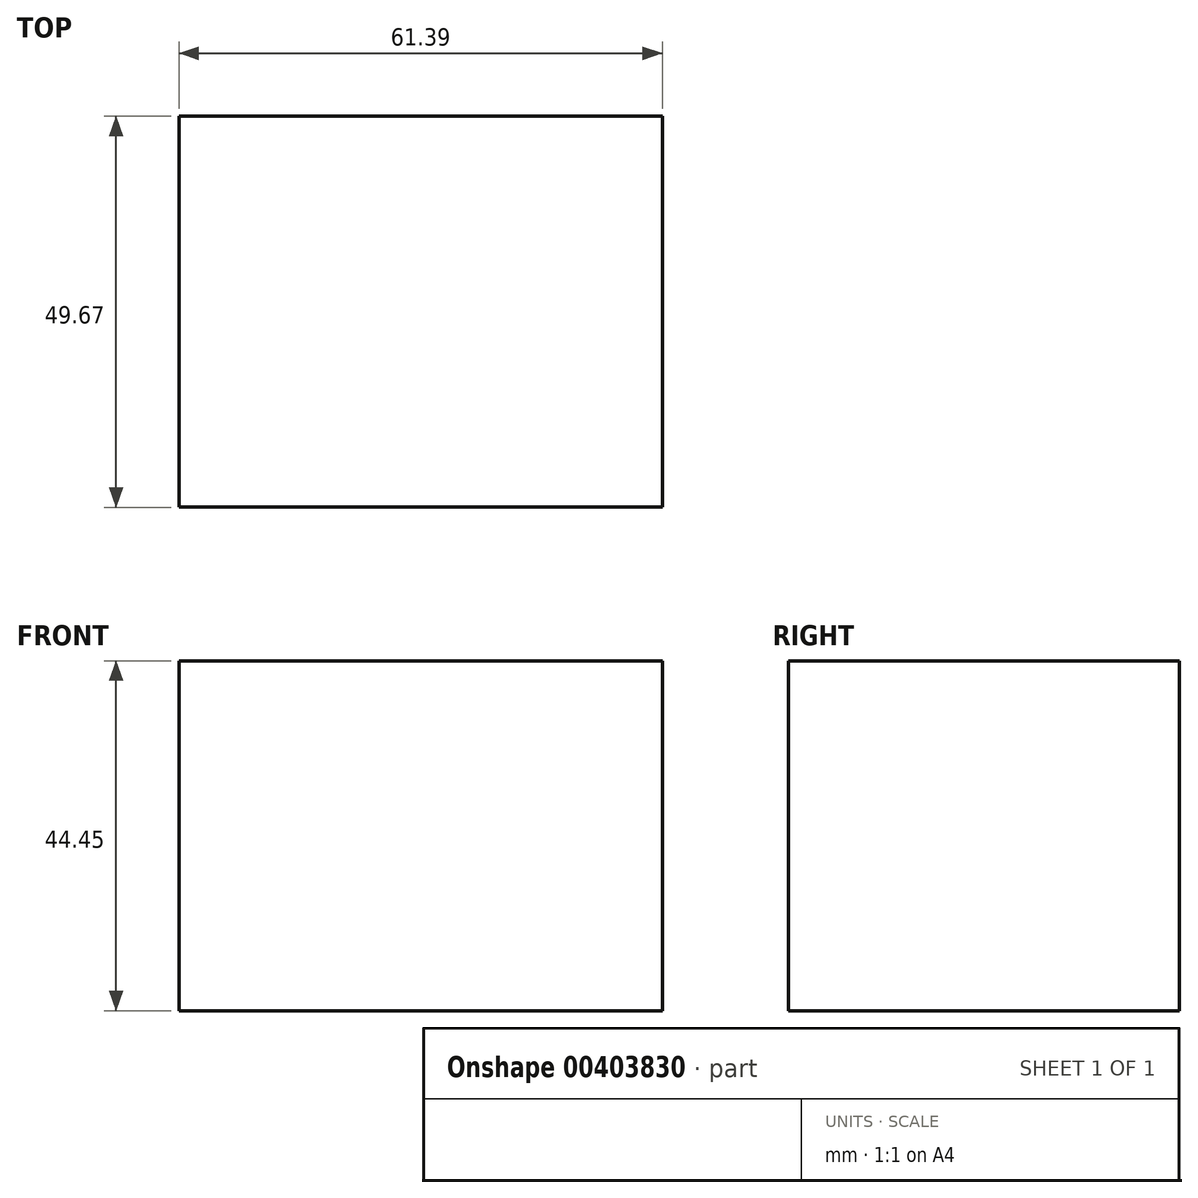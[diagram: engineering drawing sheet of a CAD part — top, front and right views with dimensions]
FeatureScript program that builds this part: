
annotation { "Feature Type Name" : "Feature", "Feature Type Description" : "" }
export const myFeature = defineFeature(function(context is Context, id is Id, definition is map)
    precondition{}
    {
        {
            var Q0;
            Q0=qCreatedBy(makeId("Top.planeOp"),FACE);
            var sketch = newSketch(context, id + "F0", { "sketchPlane" : qUnion([Q0])});
            skLineSegment(sketch, "E0.bottom", {"start": v(-30.85, -18.4) * mm, "end": v(30.54, -18.4) * mm});
            skLineSegment(sketch, "E0.top", {"start": v(-30.85, 31.26) * mm, "end": v(30.54, 31.26) * mm});
            skLineSegment(sketch, "E0.left", {"start": v(-30.85, -18.4) * mm, "end": v(-30.85, 31.26) * mm});
            skLineSegment(sketch, "E0.right", {"start": v(30.54, -18.4) * mm, "end": v(30.54, 31.26) * mm});
            skSolve(sketch);
        }
        {
            var Q0;
            Q0=makeQuery(id+"F0.imprint","IMPRINT",FACE,{"disambiguationData":[TD([[makeQuery(id+"F0.imprint","IMPRINT",EDGE,{"derivedFrom":sQuery(id+"F0.wireOp",EDGE,"E0.bottom")}),1.0]])]});
            extrude(context, id + "F1", {"entities" : qUnion([Q0]), "depth" : 44.45 * mm});
        }
    });
